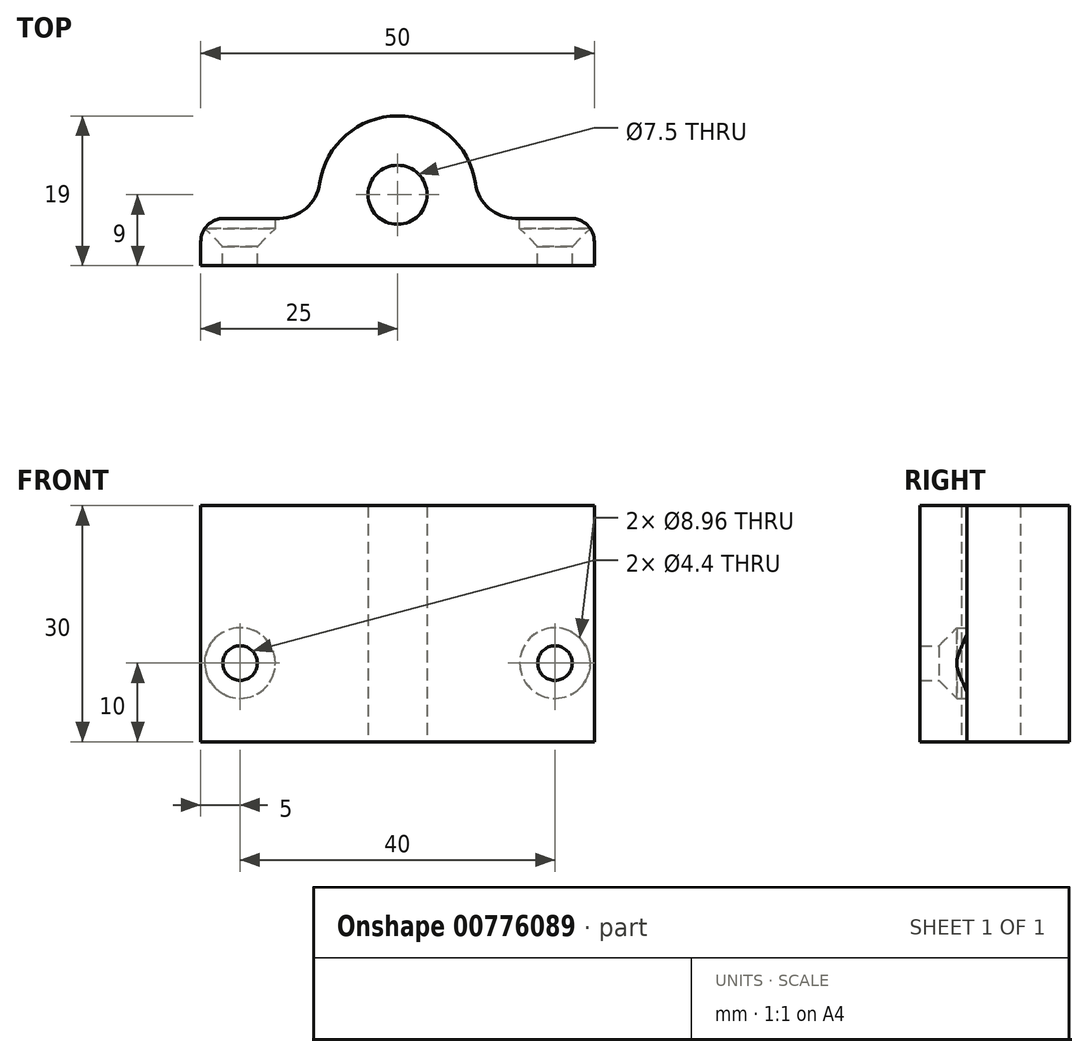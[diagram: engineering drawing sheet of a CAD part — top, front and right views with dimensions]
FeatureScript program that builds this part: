
annotation { "Feature Type Name" : "Feature", "Feature Type Description" : "" }
export const myFeature = defineFeature(function(context is Context, id is Id, definition is map)
    precondition{}
    {
        {
            var Q0;
            Q0=qCreatedBy(makeId("Top.planeOp"),FACE);
            var sketch = newSketch(context, id + "F0", { "sketchPlane" : qUnion([Q0])});
            skCircle(sketch, "E0", {"center": v(0, 0) * mm, "radius": 3.75 * mm});
            skLineSegment(sketch, "E1.top", {"start": v(25, -9) * mm, "end": v(-25, -9) * mm});
            skLineSegment(sketch, "E1.left", {"start": v(25, -6) * mm, "end": v(25, -9) * mm});
            skLineSegment(sketch, "E1.right", {"start": v(-25, -6) * mm, "end": v(-25, -9) * mm});
            skPoint(sketch, "E1.middle", {"position": v(0, -6) * mm});
            skArc(sketch, "E2", {"start": v(-9.9, 1.42) * mm, "mid": v(0, 10) * mm, "end": v(9.9, 1.42) * mm});
            skArc(sketch, "E3", {"start": v(-9.9, 1.42) * mm, "mid": v(-11.62, -1.74) * mm, "end": v(-15, -3) * mm});
            skArc(sketch, "E4", {"start": v(9.9, 1.42) * mm, "mid": v(11.62, -1.74) * mm, "end": v(15, -3) * mm});
            skLineSegment(sketch, "E5", {"start": v(-15, -3) * mm, "end": v(-22, -3) * mm});
            skLineSegment(sketch, "E6", {"start": v(15, -3) * mm, "end": v(22, -3) * mm});
            skPoint(sketch, "E7.visualSharp", {"position": v(-25, -3) * mm});
            skArc(sketch, "E7.filletArc", {"start": v(-22, -3) * mm, "mid": v(-24.12, -3.88) * mm, "end": v(-25, -6) * mm});
            skPoint(sketch, "E8.visualSharp", {"position": v(25, -3) * mm});
            skArc(sketch, "E8.filletArc", {"start": v(25, -6) * mm, "mid": v(24.12, -3.88) * mm, "end": v(22, -3) * mm});
            skSolve(sketch);
        }
        {
            var Q0;
            Q0=makeQuery(id+"F0.imprint","IMPRINT",FACE,{"disambiguationData":[TD([[makeQuery(id+"F0.imprint","IMPRINT",EDGE,{"derivedFrom":sQuery(id+"F0.wireOp",EDGE,"E0")}),-1.0]])]});
            extrude(context, id + "F1", {"entities" : qUnion([Q0]), "depth" : 20 * mm, "offsetDistance" : 25 * mm, "hasSecondDirection" : true, "secondDirectionOppositeDirection" : true, "secondDirectionDepth" : 10 * mm});
        }
        {
            var Q0;
            Q0=qCreatedBy(makeId("Front.planeOp"),FACE);
            var sketch = newSketch(context, id + "F2", { "sketchPlane" : qUnion([Q0])});
            skLineSegment(sketch, "E9", {"start": v(-20, 0) * mm, "end": v(20, 0) * mm});
            skSolve(sketch);
        }
        {
            var Q0;
            Q0=sQuery(id+"F2.wireOp",VERTEX,"E9.start");
            var Q1;
            Q1=sQuery(id+"F2.wireOp",VERTEX,"E9.end");
            var Q2;
            Q2=makeQuery(id+"F1.opExtrude","SWEPT_BODY",BODY,{"disambiguationData":[OSD([sQuery(id+"F0.wireOp",EDGE,"E0"),sQuery(id+"F0.wireOp",EDGE,"E1.top"),sQuery(id+"F0.wireOp",EDGE,"E1.left"),sQuery(id+"F0.wireOp",EDGE,"E1.right"),sQuery(id+"F0.wireOp",EDGE,"E2"),sQuery(id+"F0.wireOp",EDGE,"E3"),sQuery(id+"F0.wireOp",EDGE,"E4"),sQuery(id+"F0.wireOp",EDGE,"E5"),sQuery(id+"F0.wireOp",EDGE,"E6"),sQuery(id+"F0.wireOp",EDGE,"E7.filletArc"),sQuery(id+"F0.wireOp",EDGE,"E8.filletArc")])]});
            hole(context, id + "F3", {"style" : HoleStyle.C_SINK, "endStyle" : HoleEndStyle.THROUGH, "oppositeDirection" : true, "standardTappedOrClearance" : lookupTablePath({ "standard" : "ISO", "fit" : "Normal", "size" : "M4", "type" : "Clearance" }), "standardBlindInLast" : lookupTablePath({ "fit" : "Standard", "standard" : "ISO", "size" : "M4", "type" : "Clearance" }), "holeDiameter" : 4.4 * mm, "cSinkDiameter" : 8.96 * mm, "cSinkAngle" : 90 * degree, "majorDiameter" : 5 * mm, "isTappedThrough" : true, "tappedDepth" : 12 * mm, "tapClearance" : 3, "locations" : qUnion([Q0, Q1]), "scope" : qUnion([Q2])});
        }
    });
